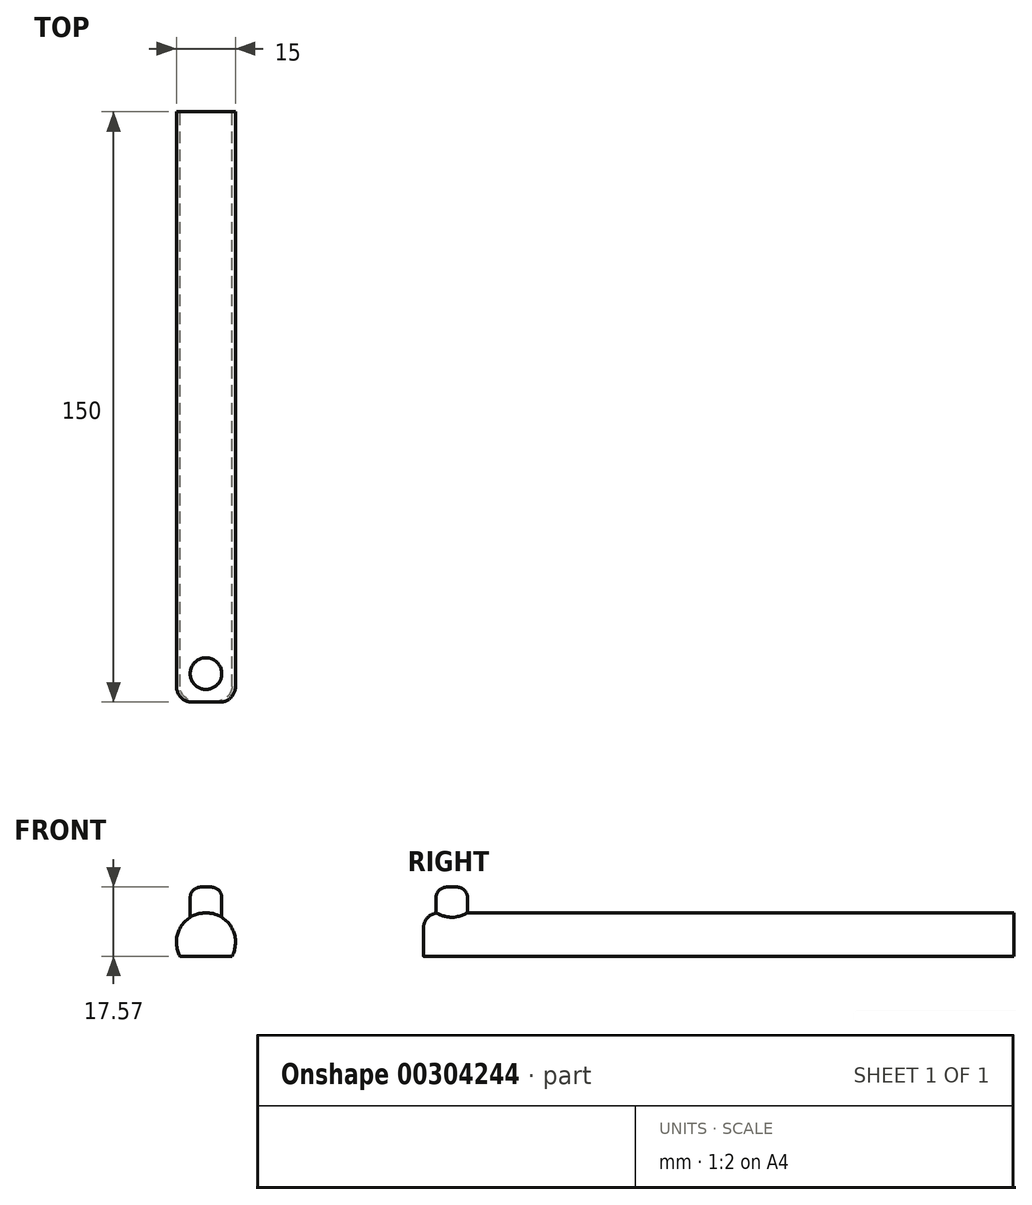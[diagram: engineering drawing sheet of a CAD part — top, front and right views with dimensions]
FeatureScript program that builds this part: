
annotation { "Feature Type Name" : "Feature", "Feature Type Description" : "" }
export const myFeature = defineFeature(function(context is Context, id is Id, definition is map)
    precondition{}
    {
        {
            var Q0;
            Q0=qCreatedBy(makeId("Front.planeOp"),FACE);
            var sketch = newSketch(context, id + "F0", { "sketchPlane" : qUnion([Q0])});
            skArc(sketch, "E0", {"start": v(6.6, -3.57) * mm, "mid": v(0, 7.5) * mm, "end": v(-6.6, -3.57) * mm});
            skLineSegment(sketch, "E1", {"start": v(-6.6, -3.57) * mm, "end": v(6.6, -3.57) * mm});
            skSolve(sketch);
        }
        {
            var Q0;
            Q0=makeQuery(id+"F0.imprint","IMPRINT",FACE,{"disambiguationData":[TD([[makeQuery(id+"F0.imprint","IMPRINT",EDGE,{"derivedFrom":sQuery(id+"F0.wireOp",EDGE,"E0")}),1.0]])]});
            extrude(context, id + "F1", {"entities" : qUnion([Q0]), "depth" : 150 * mm});
        }
        {
            var Q0;
            Q0=qCreatedBy(makeId("Top.planeOp"),FACE);
            var sketch = newSketch(context, id + "F2", { "sketchPlane" : qUnion([Q0])});
            skCircle(sketch, "E2", {"center": v(0, -142.76) * mm, "radius": 4.01 * mm});
            skSolve(sketch);
        }
        {
            var Q0;
            Q0 = qSketchRegion(id + "F2", true);
            extrude(context, id + "F3", {"entities" : qUnion([Q0]), "operationType" : NewBodyOperationType.ADD, "depth" : 14 * mm});
        }
        {
            var Q0;
            Q0=makeQuery(id+"F1.opExtrude","CAP_EDGE",EDGE,{"disambiguationData":[OSD([sQuery(id+"F0.wireOp",EDGE,"E0")])],"isStart":false});
            fillet(context, id + "F4", {"entities" : qUnion([Q0]), "radius" : 4 * mm, "tangentPropagation" : true, "allowEdgeOverflow" : false});
        }
        {
            var Q0;
            Q0=makeQuery(id+"F3.opExtrude","CAP_EDGE",EDGE,{"disambiguationData":[OSD([sQuery(id+"F2.wireOp",EDGE,"E2")])],"isStart":false});
            fillet(context, id + "F5", {"entities" : qUnion([Q0]), "radius" : 2.73 * mm, "tangentPropagation" : true, "allowEdgeOverflow" : false});
        }
    });
